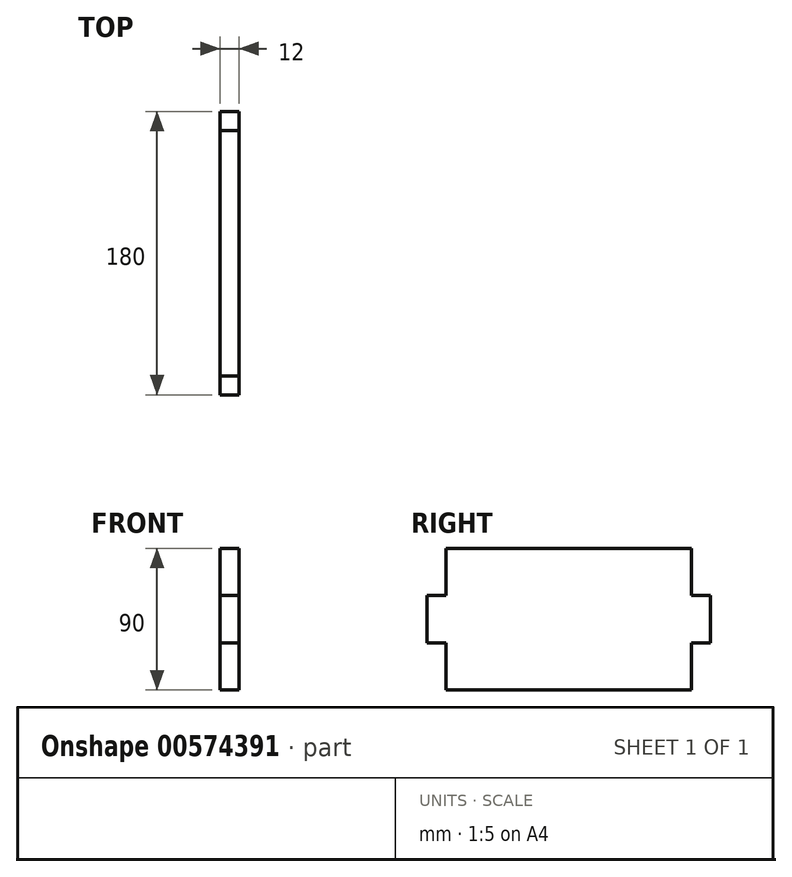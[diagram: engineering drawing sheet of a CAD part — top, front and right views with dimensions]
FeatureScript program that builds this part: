
annotation { "Feature Type Name" : "Feature", "Feature Type Description" : "" }
export const myFeature = defineFeature(function(context is Context, id is Id, definition is map)
    precondition{}
    {
        {
            var Q0;
            Q0=qCreatedBy(makeId("Right.planeOp"),FACE);
            var sketch = newSketch(context, id + "F0", { "sketchPlane" : qUnion([Q0])});
            skLineSegment(sketch, "E0", {"start": v(0, 0) * mm, "end": v(0, 30) * mm});
            skLineSegment(sketch, "E1", {"start": v(0, 30) * mm, "end": v(-12, 30) * mm});
            skLineSegment(sketch, "E2", {"start": v(-12, 30) * mm, "end": v(-12, 60) * mm});
            skLineSegment(sketch, "E3", {"start": v(-12, 60) * mm, "end": v(0, 60) * mm});
            skLineSegment(sketch, "E4", {"start": v(0, 60) * mm, "end": v(0, 90) * mm});
            skPoint(sketch, "E4.endSnap0", {"position": v(0, 15) * mm});
            skLineSegment(sketch, "E5", {"start": v(0, 90) * mm, "end": v(78, 90) * mm});
            skLineSegment(sketch, "E6", {"start": v(78, 90) * mm, "end": v(78, 0) * mm, "construction": true});
            skLineSegment(sketch, "E7", {"start": v(78, 0) * mm, "end": v(0, 0) * mm});
            skLineSegment(sketch, "E8.MirrorCS", {"start": v(78, 0) * mm, "end": v(156, 0) * mm});
            skPoint(sketch, "E9.MirrorP", {"position": v(156, 15) * mm});
            skLineSegment(sketch, "E10.MirrorCS", {"start": v(156, 30) * mm, "end": v(168, 30) * mm});
            skLineSegment(sketch, "E11.MirrorCS", {"start": v(168, 30) * mm, "end": v(168, 60) * mm});
            skLineSegment(sketch, "E12.MirrorCS", {"start": v(168, 60) * mm, "end": v(156, 60) * mm});
            skLineSegment(sketch, "E13.MirrorCS", {"start": v(156, 60) * mm, "end": v(156, 90) * mm});
            skLineSegment(sketch, "E14.MirrorCS", {"start": v(156, 0) * mm, "end": v(156, 30) * mm});
            skLineSegment(sketch, "E15.MirrorCS", {"start": v(156, 90) * mm, "end": v(78, 90) * mm});
            skSolve(sketch);
        }
        {
            var Q0;
            Q0=makeQuery(id+"F0.imprint","IMPRINT",FACE,{"disambiguationData":[TD([[makeQuery(id+"F0.imprint","IMPRINT",EDGE,{"derivedFrom":sQuery(id+"F0.wireOp",EDGE,"E0")}),-1.0]])]});
            extrude(context, id + "F1", {"entities" : qUnion([Q0]), "depth" : 12 * mm, "offsetDistance" : 25 * mm});
        }
    });
